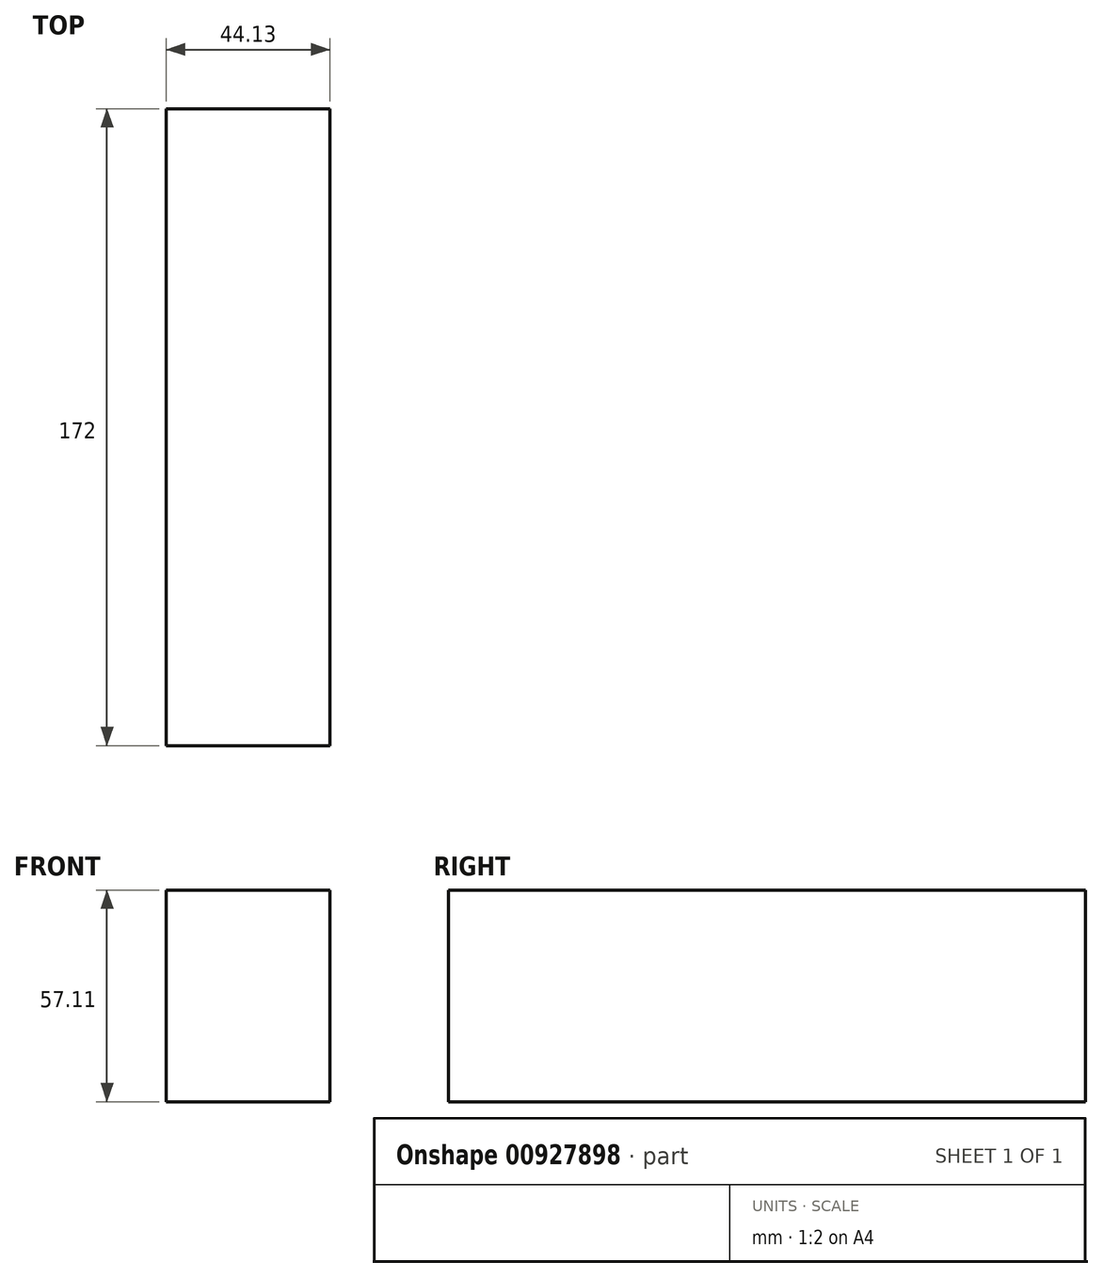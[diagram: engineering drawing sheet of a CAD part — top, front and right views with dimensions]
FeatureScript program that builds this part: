
annotation { "Feature Type Name" : "Feature", "Feature Type Description" : "" }
export const myFeature = defineFeature(function(context is Context, id is Id, definition is map)
    precondition{}
    {
        {
            var Q0;
            Q0=qCreatedBy(makeId("Front.planeOp"),FACE);
            var sketch = newSketch(context, id + "F0", { "sketchPlane" : qUnion([Q0])});
            skLineSegment(sketch, "E0.bottom", {"start": v(-93.66, 42.66) * mm, "end": v(-49.53, 42.66) * mm});
            skLineSegment(sketch, "E0.top", {"start": v(-93.66, -14.45) * mm, "end": v(-49.53, -14.45) * mm});
            skLineSegment(sketch, "E0.left", {"start": v(-93.66, 42.66) * mm, "end": v(-93.66, -14.45) * mm});
            skLineSegment(sketch, "E0.right", {"start": v(-49.53, 42.66) * mm, "end": v(-49.53, -14.45) * mm});
            skSolve(sketch);
        }
        {
            var Q0;
            Q0 = qSketchRegion(id + "F0", true);
            extrude(context, id + "F1", {"entities" : qUnion([Q0]), "depth" : 172 * mm, "offsetDistance" : 25 * mm});
        }
    });
